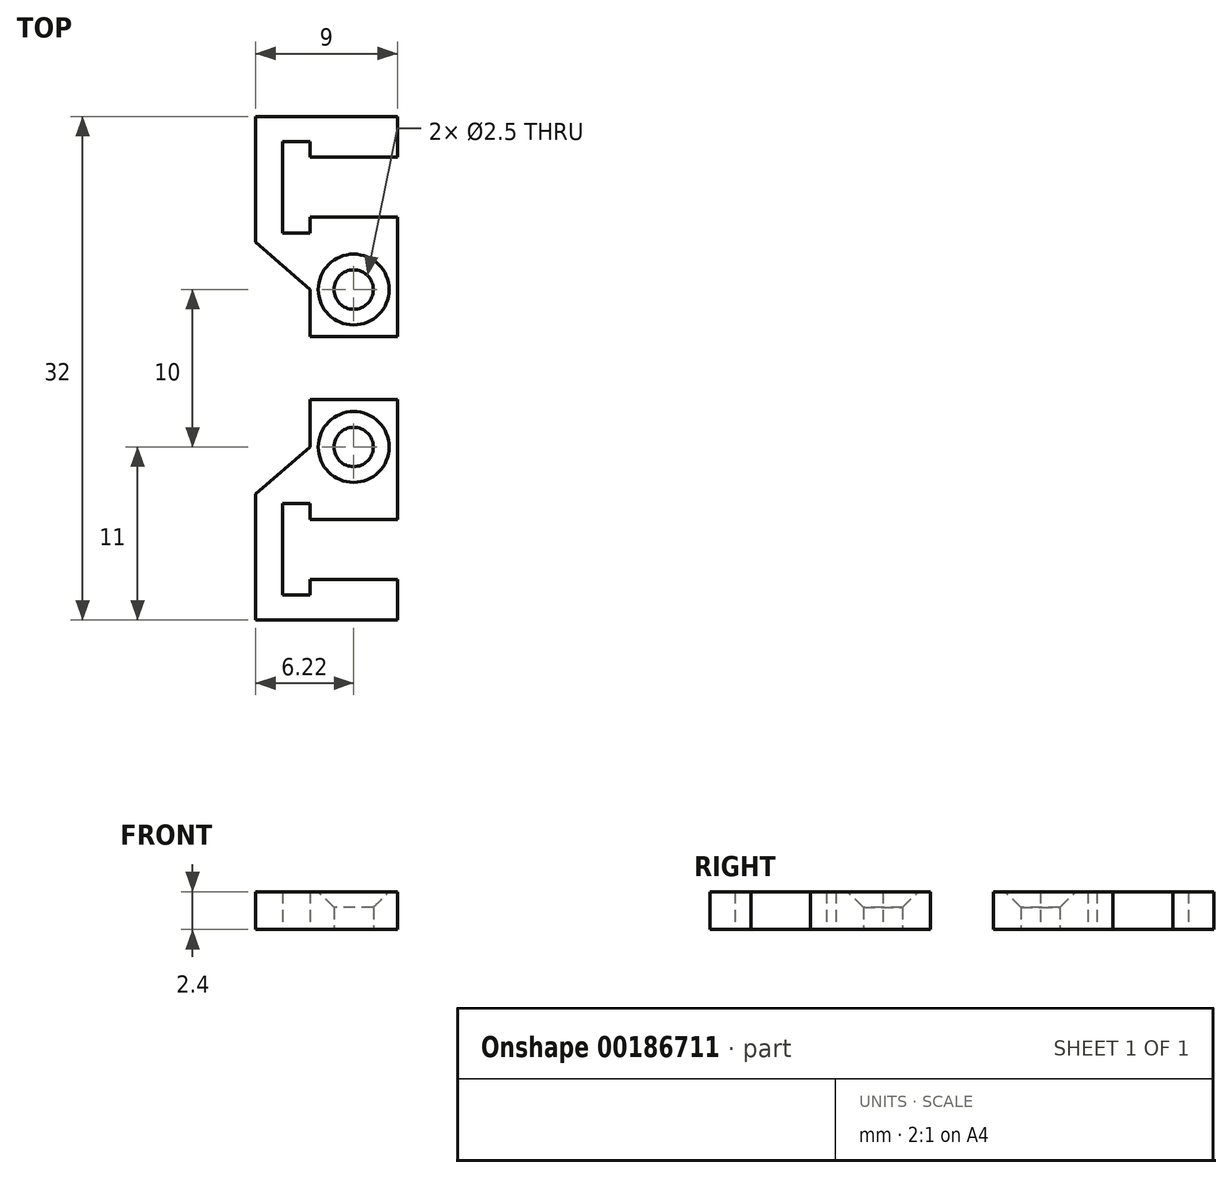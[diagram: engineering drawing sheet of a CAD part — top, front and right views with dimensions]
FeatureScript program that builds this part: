
annotation { "Feature Type Name" : "Feature", "Feature Type Description" : "" }
export const myFeature = defineFeature(function(context is Context, id is Id, definition is map)
    precondition{}
    {
        {
            var Q0;
            Q0=qCreatedBy(makeId("Top.planeOp"),FACE);
            var sketch = newSketch(context, id + "F0", { "sketchPlane" : qUnion([Q0])});
            skCircle(sketch, "E0", {"center": v(0, 0) * mm, "radius": 1.25 * mm});
            skLineSegment(sketch, "E1.top", {"start": v(2.77, -3) * mm, "end": v(-2.77, -3) * mm});
            skLineSegment(sketch, "E1.left", {"start": v(2.77, 3) * mm, "end": v(2.78, -3) * mm});
            skLineSegment(sketch, "E1.right", {"start": v(-2.77, 0) * mm, "end": v(-2.77, -3) * mm});
            skLineSegment(sketch, "E2", {"start": v(2.77, 3) * mm, "end": v(2.77, 11) * mm});
            skLineSegment(sketch, "E3", {"start": v(2.77, 11) * mm, "end": v(-6.23, 11) * mm});
            skLineSegment(sketch, "E4", {"start": v(-6.23, 11) * mm, "end": v(-6.23, 3) * mm});
            skLineSegment(sketch, "E5", {"start": v(-6.23, 3) * mm, "end": v(-2.77, 0) * mm});
            skLineSegment(sketch, "E6", {"start": v(-2.78, 3.6) * mm, "end": v(-2.78, 4.6) * mm});
            skLineSegment(sketch, "E7", {"start": v(-2.77, 9.4) * mm, "end": v(-4.52, 9.4) * mm});
            skLineSegment(sketch, "E8", {"start": v(-4.52, 9.4) * mm, "end": v(-4.52, 3.6) * mm});
            skLineSegment(sketch, "E9", {"start": v(-4.52, 3.6) * mm, "end": v(-2.77, 3.6) * mm});
            skLineSegment(sketch, "E10", {"start": v(-2.77, 8.4) * mm, "end": v(2.77, 8.4) * mm});
            skLineSegment(sketch, "E11", {"start": v(-2.77, 4.6) * mm, "end": v(2.77, 4.6) * mm});
            skLineSegment(sketch, "E12.trimOffspring", {"start": v(-2.78, 8.4) * mm, "end": v(-2.78, 9.4) * mm});
            skPoint(sketch, "E13.orphan", {"position": v(-2.77, 3) * mm});
            skSolve(sketch);
        }
        {
            var Q0;
            Q0=makeQuery(id+"F0.imprint","IMPRINT",FACE,{"disambiguationData":[TD([[makeQuery(id+"F0.imprint","IMPRINT",EDGE,{"derivedFrom":sQuery(id+"F0.wireOp",EDGE,"E0")}),-1.0]])]});
            extrude(context, id + "F1", {"entities" : qUnion([Q0]), "depth" : 2.4 * mm});
        }
        {
            var Q0;
            Q0=makeQuery(id+"F1.opExtrude","CAP_EDGE",EDGE,{"disambiguationData":[OSD([sQuery(id+"F0.wireOp",EDGE,"E0")])],"isStart":false});
            chamfer(context, id + "F2", {"entities" : qUnion([Q0]), "width" : 1 * mm, "tangentPropagation" : true});
        }
        {
            var Q0;
            Q0=qCreatedBy(makeId("Front.planeOp"),FACE);
            cPlane(context, id + "F3", {"entities" : qUnion([Q0]), "cplaneType" : CPlaneType.OFFSET, "offset" : 5 * mm, "width" : 150 * mm, "height" : 150 * mm});
        }
        {
            var Q0;
            Q0=makeQuery(id+"F1.opExtrude","SWEPT_BODY",BODY,{"disambiguationData":[OSD([sQuery(id+"F0.wireOp",EDGE,"E0"),sQuery(id+"F0.wireOp",EDGE,"E1.top"),sQuery(id+"F0.wireOp",EDGE,"E1.left"),sQuery(id+"F0.wireOp",EDGE,"E1.right"),sQuery(id+"F0.wireOp",EDGE,"E2"),sQuery(id+"F0.wireOp",EDGE,"E3"),sQuery(id+"F0.wireOp",EDGE,"E4"),sQuery(id+"F0.wireOp",EDGE,"E5"),sQuery(id+"F0.wireOp",EDGE,"E6"),sQuery(id+"F0.wireOp",EDGE,"E7"),sQuery(id+"F0.wireOp",EDGE,"E8"),sQuery(id+"F0.wireOp",EDGE,"E9"),sQuery(id+"F0.wireOp",EDGE,"E10"),sQuery(id+"F0.wireOp",EDGE,"E11"),sQuery(id+"F0.wireOp",EDGE,"E12.trimOffspring")])]});
            var Q1;
            Q1=qCreatedBy(id+"F3.planeOp",FACE);
            mirror(context, id + "F4", {"entities" : qUnion([Q0]), "mirrorPlane" : qUnion([Q1])});
        }
    });
